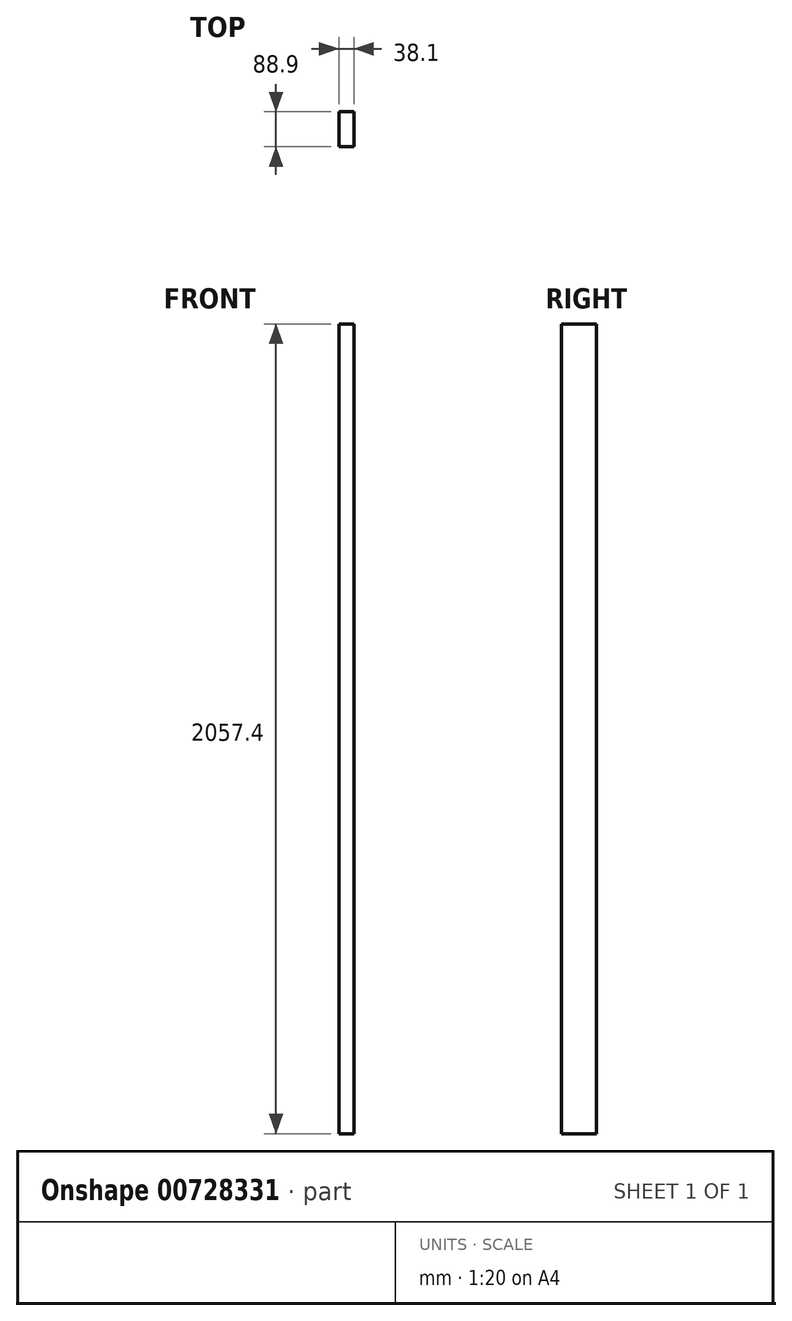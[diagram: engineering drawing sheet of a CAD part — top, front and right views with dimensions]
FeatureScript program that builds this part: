
annotation { "Feature Type Name" : "Feature", "Feature Type Description" : "" }
export const myFeature = defineFeature(function(context is Context, id is Id, definition is map)
    precondition{}
    {
        {
            var Q0;
            Q0=qCreatedBy(makeId("Front.planeOp"),FACE);
            var sketch = newSketch(context, id + "F0", { "sketchPlane" : qUnion([Q0])});
            skLineSegment(sketch, "E0.bottom", {"start": v(19.05, -1028.7) * mm, "end": v(-19.05, -1028.7) * mm});
            skLineSegment(sketch, "E0.top", {"start": v(19.05, 1028.7) * mm, "end": v(-19.05, 1028.7) * mm});
            skLineSegment(sketch, "E0.left", {"start": v(19.05, -1028.7) * mm, "end": v(19.05, 1028.7) * mm});
            skLineSegment(sketch, "E0.right", {"start": v(-19.05, -1028.7) * mm, "end": v(-19.05, 1028.7) * mm});
            skPoint(sketch, "E0.middle", {"position": v(0, 0) * mm});
            skSolve(sketch);
        }
        {
            var Q0;
            Q0=qSketchRegion(id+"F0",true);
            extrude(context, id + "F1", {"entities" : qUnion([Q0]), "depth" : 88.9 * mm});
        }
    });
